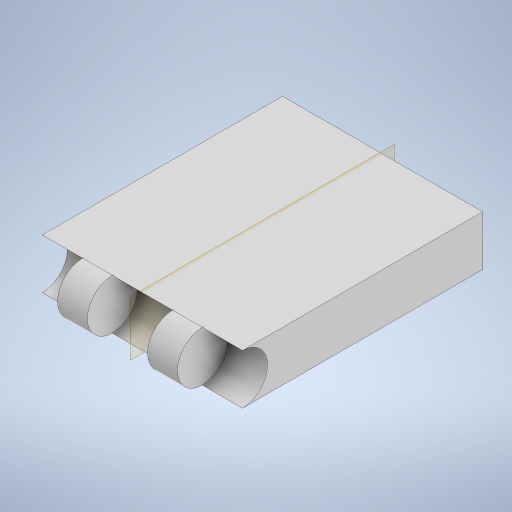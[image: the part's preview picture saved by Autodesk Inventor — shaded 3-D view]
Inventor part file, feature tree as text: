
AUTODESK INVENTOR PART (.ipt)
format: ipt  version: 2024.2 (Build 282272000, 272)  size: 257,024 bytes
history: native  units: in
note: dims shown in document units (in); Inventor stores cm internally (conversion verified against a paired STEP export)
features: sketch x4, extrude x2, revolve x2, plane x1, mirror x1
ambient origin geometry x8: Origin, YZ Plane, XZ Plane, XY Plane, X Axis, Y Axis, Z Axis, Center Point
bodies: Solid1 (feature_tree)
feature tree (10):
  extrude  "Extrusion1"  Depth=3.0in
  extrude  "Extrusion2"  Depth=0.5in TaperAngle=0.0deg
  plane  "Work Plane1"
  mirror  "Mirror1"
  revolve  "Revolution1"  [1 undecoded]
  revolve  "Revolution2"  Angle=90.0deg
  sketch  "Sketch1"  dims[d0=2.5in d1=3.0in]
  sketch  "Sketch2"  dims[d2=0.625in d3=0.0in d5=0.5in d6=0.0in]
  sketch  "Sketch3"  dims[d7=-1.25in d8=0.75in]
  sketch  "Sketch4"  dims[d9=0.375in d10=90.0deg d11=90.0deg]
note: 1 required parameter value undecoded (feature->parameter linkage not recoverable at this tier; creation-order binding heuristic only, values carry confidence <= 0.55)
